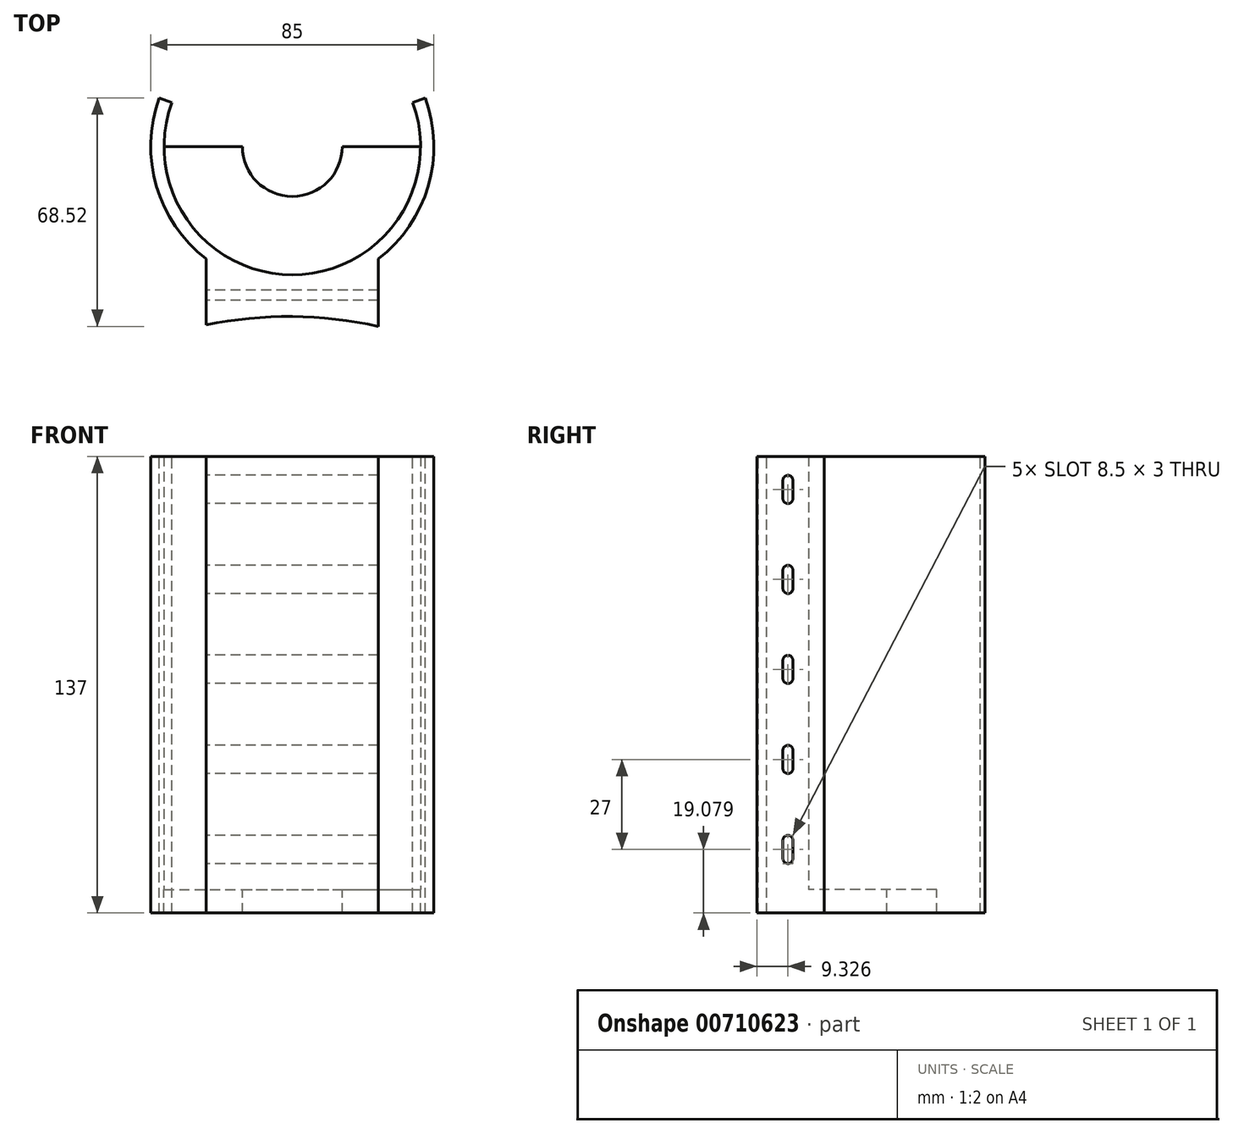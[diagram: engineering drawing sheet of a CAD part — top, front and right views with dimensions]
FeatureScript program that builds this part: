
annotation { "Feature Type Name" : "Feature", "Feature Type Description" : "" }
export const myFeature = defineFeature(function(context is Context, id is Id, definition is map)
    precondition{}
    {
        {
            var Q0;
            Q0=qCreatedBy(makeId("Top.planeOp"),FACE);
            var sketch = newSketch(context, id + "F0", { "sketchPlane" : qUnion([Q0])});
            skCircle(sketch, "E0", {"center": v(0, 0) * mm, "radius": 42.5 * mm});
            skSolve(sketch);
        }
        {
            var Q0;
            Q0=qSketchRegion(id+"F0",true);
            extrude(context, id + "F1", {"entities" : qUnion([Q0]), "depth" : 7 * mm, "offsetDistance" : 25 * mm});
        }
        {
            var Q0;
            Q0=makeQuery(id+"F1.opExtrude","CAP_FACE",FACE,{"disambiguationData":[OSD([sQuery(id+"F0.wireOp",EDGE,"E0")])],"isStart":false});
            var sketch = newSketch(context, id + "F2", { "sketchPlane" : qUnion([Q0])});
            skCircle(sketch, "E1", {"center": v(0, 0) * mm, "radius": 15 * mm});
            skSolve(sketch);
        }
        {
            var Q0;
            Q0=makeQuery(id+"F2.imprint","IMPRINT",FACE,{"disambiguationData":[TD([[makeQuery(id+"F2.imprint","IMPRINT",EDGE,{"derivedFrom":sQuery(id+"F2.wireOp",EDGE,"E1")}),1.0]])]});
            extrude(context, id + "F3", {"entities" : qUnion([Q0]), "operationType" : NewBodyOperationType.REMOVE, "oppositeDirection" : true, "depth" : 25 * mm, "offsetDistance" : 25 * mm});
        }
        {
            var Q0;
            Q0=makeQuery(id+"F1.opExtrude","CAP_FACE",FACE,{"disambiguationData":[OSD([sQuery(id+"F0.wireOp",EDGE,"E0")])],"isStart":false});
            var sketch = newSketch(context, id + "F4", { "sketchPlane" : qUnion([Q0])});
            skCircle(sketch, "E2", {"center": v(0, 0) * mm, "radius": 38.5 * mm});
            skCircle(sketch, "E3", {"center": v(0, 0) * mm, "radius": 42.5 * mm});
            skSolve(sketch);
        }
        {
            var Q0;
            Q0=qSketchRegion(id+"F4",true);
            extrude(context, id + "F5", {"entities" : qUnion([Q0]), "operationType" : NewBodyOperationType.ADD, "depth" : 130 * mm, "offsetDistance" : 25 * mm});
        }
        {
            var Q0;
            Q0=makeQuery(id+"F5.opExtrude","CAP_FACE",FACE,{"disambiguationData":[OSD([sQuery(id+"F4.wireOp",EDGE,"E2"),sQuery(id+"F4.wireOp",EDGE,"E3")])],"isStart":false});
            var sketch = newSketch(context, id + "F6", { "sketchPlane" : qUnion([Q0])});
            skCircle(sketch, "E4.0", {"center": v(0, 0) * mm, "radius": 38.5 * mm});
            skCircle(sketch, "E5.0", {"center": v(0, 0) * mm, "radius": 42.5 * mm});
            skLineSegment(sketch, "E6", {"start": v(-39.94, -14.54) * mm, "end": v(-35.24, -12.83) * mm});
            skLineSegment(sketch, "E7", {"start": v(0, 0) * mm, "end": v(0, 42.5) * mm});
            skLineSegment(sketch, "E8.MirrorCS", {"start": v(-39.94, 14.54) * mm, "end": v(-35.24, 12.83) * mm});
            skLineSegment(sketch, "E9", {"start": v(0, 0) * mm, "end": v(-42.5, 0) * mm});
            skLineSegment(sketch, "E10.MirrorCS", {"start": v(-14.54, -39.94) * mm, "end": v(-12.83, -35.24) * mm});
            skLineSegment(sketch, "E11.MirrorCS", {"start": v(14.54, -39.94) * mm, "end": v(12.83, -35.24) * mm});
            skLineSegment(sketch, "E12.MirrorCS", {"start": v(39.94, 14.54) * mm, "end": v(35.24, 12.83) * mm});
            skLineSegment(sketch, "E13.MirrorCS", {"start": v(39.94, -14.54) * mm, "end": v(35.24, -12.83) * mm});
            skLineSegment(sketch, "E14.MirrorCS", {"start": v(-14.54, 39.94) * mm, "end": v(-12.83, 35.24) * mm});
            skLineSegment(sketch, "E15.MirrorCS", {"start": v(14.54, 39.94) * mm, "end": v(12.83, 35.24) * mm});
            skSolve(sketch);
        }
        {
            var Q0;
            {var subQ0=sQuery(id+"F6.wireOp",EDGE,"E8.MirrorCS");Q0=makeQuery(id+"F6.imprint","IMPRINT",FACE,{"disambiguationData":[TD([[makeQuery(id+"F6.imprint","IMPRINT",EDGE,{"derivedFrom":subQ0}),1.0]])]});}
            var Q1;
            {var subQ0=sQuery(id+"F6.wireOp",EDGE,"E15.MirrorCS");var subQ1=sQuery(id+"F6.wireOp",EDGE,"E4.0");var subQ2=makeQuery(id+"F6.imprint","INTERSECT",VERTEX,{"derivedFrom":[subQ1,subQ0]});Q1=makeQuery(id+"F6.imprint","IMPRINT",FACE,{"disambiguationData":[TD([[makeQuery(id+"F6.imprint","IMPRINT",EDGE,{"disambiguationData":[TD([[subQ2,1.0]])],"derivedFrom":subQ1}),-1.0]])]});}
            var Q2;
            {var subQ0=sQuery(id+"F6.wireOp",EDGE,"E15.MirrorCS");var subQ1=sQuery(id+"F6.wireOp",EDGE,"E4.0");var subQ2=makeQuery(id+"F6.imprint","INTERSECT",VERTEX,{"derivedFrom":[subQ1,subQ0]});Q2=makeQuery(id+"F6.imprint","IMPRINT",FACE,{"disambiguationData":[TD([[makeQuery(id+"F6.imprint","IMPRINT",EDGE,{"disambiguationData":[TD([[subQ2,-1.0]])],"derivedFrom":subQ1}),-1.0]])]});}
            var Q3;
            {var subQ0=sQuery(id+"F6.wireOp",EDGE,"E14.MirrorCS");var subQ1=sQuery(id+"F6.wireOp",EDGE,"E4.0");var subQ2=makeQuery(id+"F6.imprint","INTERSECT",VERTEX,{"derivedFrom":[subQ1,subQ0]});Q3=makeQuery(id+"F6.imprint","IMPRINT",FACE,{"disambiguationData":[TD([[makeQuery(id+"F6.imprint","IMPRINT",EDGE,{"disambiguationData":[TD([[subQ2,1.0]])],"derivedFrom":subQ1}),-1.0]])]});}
            var Q4;
            Q4=makeQuery(id+"F1.opExtrude","CAP_FACE",FACE,{"disambiguationData":[OSD([sQuery(id+"F0.wireOp",EDGE,"E0")])],"isStart":false});
            extrude(context, id + "F7", {"entities" : qUnion([Q0, Q1, Q2, Q3]), "operationType" : NewBodyOperationType.REMOVE, "endBound" : BoundingType.UP_TO_SURFACE, "oppositeDirection" : true, "depth" : 25 * mm, "endBoundEntityFace" : qUnion([Q4]), "offsetDistance" : 25 * mm});
        }
        {
            var Q0;
            Q0=makeQuery(id+"F5.opExtrude","CAP_FACE",FACE,{"disambiguationData":[OSD([sQuery(id+"F4.wireOp",EDGE,"E2"),sQuery(id+"F4.wireOp",EDGE,"E3")])],"isStart":false});
            var sketch = newSketch(context, id + "F8", { "sketchPlane" : qUnion([Q0])});
            skLineSegment(sketch, "E16", {"start": v(-44.89, 0) * mm, "end": v(48.54, 0) * mm});
            skLineSegment(sketch, "E17", {"start": v(48.54, 0) * mm, "end": v(48.54, 50.13) * mm});
            skLineSegment(sketch, "E18", {"start": v(48.54, 50.13) * mm, "end": v(-44.89, 50.13) * mm});
            skLineSegment(sketch, "E19", {"start": v(-44.89, 50.13) * mm, "end": v(-44.89, 0) * mm});
            skSolve(sketch);
        }
        {
            var Q0;
            {var subQ9=sQuery(id+"F8.wireOp",EDGE,"E17");Q0=makeQuery(id+"F8.imprint","IMPRINT",FACE,{"disambiguationData":[TD([[makeQuery(id+"F8.imprint","IMPRINT",EDGE,{"derivedFrom":subQ9}),1.0]])]});}
            var Q1;
            {var subQ5=makeQuery(id+"F7.boolean.opBoolean","COPY",EDGE,{"derivedFrom":makeQuery(id+"F7.opExtrude","CAP_EDGE",EDGE,{"disambiguationData":[OSD([sQuery(id+"F6.wireOp",EDGE,"E8.MirrorCS")])],"isStart":true})});Q1=makeQuery(id+"F8.imprint","IMPRINT",FACE,{"disambiguationData":[TD([[makeQuery(id+"F8.imprint","IMPRINT",EDGE,{"derivedFrom":subQ5}),-1.0]])]});}
            var Q2;
            {var subQ5=makeQuery(id+"F7.boolean.opBoolean","COPY",EDGE,{"derivedFrom":makeQuery(id+"F7.opExtrude","CAP_EDGE",EDGE,{"disambiguationData":[OSD([sQuery(id+"F6.wireOp",EDGE,"E12.MirrorCS")])],"isStart":true})});Q2=makeQuery(id+"F8.imprint","IMPRINT",FACE,{"disambiguationData":[TD([[makeQuery(id+"F8.imprint","IMPRINT",EDGE,{"derivedFrom":subQ5}),1.0]])]});}
            extrude(context, id + "F9", {"entities" : qUnion([Q0, Q1, Q2]), "operationType" : NewBodyOperationType.REMOVE, "endBound" : BoundingType.THROUGH_ALL, "oppositeDirection" : true, "depth" : 25 * mm, "offsetDistance" : 25 * mm});
        }
        {
            var Q0;
            Q0=makeQuery(id+"F5.opExtrude","CAP_FACE",FACE,{"disambiguationData":[OSD([sQuery(id+"F4.wireOp",EDGE,"E2"),sQuery(id+"F4.wireOp",EDGE,"E3")])],"isStart":false});
            var sketch = newSketch(context, id + "F10", { "sketchPlane" : qUnion([Q0])});
            skArc(sketch, "E20.0", {"start": v(-25.84, -33.74) * mm, "mid": v(18.81, -38.1) * mm, "end": v(42.5, 0) * mm});
            skLineSegment(sketch, "E21.0", {"start": v(-25.84, -33.74) * mm, "end": v(-25.84, -53.5) * mm});
            skPoint(sketch, "E22.orphan", {"position": v(-42.5, 0) * mm});
            skLineSegment(sketch, "E23.MirrorCS", {"start": v(25.84, -33.74) * mm, "end": v(25.84, -53.98) * mm});
            skArc(sketch, "E24", {"start": v(25.84, -53.98) * mm, "mid": v(0.02, -51.03) * mm, "end": v(-25.84, -53.5) * mm});
            skSolve(sketch);
        }
        {
            var Q0;
            Q0=qSketchRegion(id+"F10",true);
            var Q1;
            Q1=makeQuery(id+"F1.opExtrude","CAP_FACE",FACE,{"disambiguationData":[OSD([sQuery(id+"F0.wireOp",EDGE,"E0")])],"isStart":true});
            extrude(context, id + "F11", {"entities" : qUnion([Q0]), "operationType" : NewBodyOperationType.ADD, "endBound" : BoundingType.UP_TO_SURFACE, "oppositeDirection" : true, "depth" : 47.1 * mm, "endBoundEntityFace" : qUnion([Q1]), "offsetDistance" : 25 * mm});
        }
        {
            var Q0;
            Q0=makeQuery(id+"F11.opExtrude","SWEPT_FACE",FACE,{"disambiguationData":[OSD([sQuery(id+"F10.wireOp",EDGE,"E21.0")])]});
            var sketch = newSketch(context, id + "F12", { "sketchPlane" : qUnion([Q0])});
            skLineSegment(sketch, "E25", {"start": v(46.15, 129.83) * mm, "end": v(46.15, 124.33) * mm});
            skLineSegment(sketch, "E26.0", {"start": v(43.15, 129.83) * mm, "end": v(43.15, 124.33) * mm});
            skArc(sketch, "E27", {"start": v(46.15, 129.83) * mm, "mid": v(44.65, 131.33) * mm, "end": v(43.15, 129.83) * mm});
            skArc(sketch, "E28", {"start": v(43.15, 124.33) * mm, "mid": v(44.65, 122.83) * mm, "end": v(46.15, 124.33) * mm});
            skArc(sketch, "E29.1.0.0", {"start": v(46.15, 102.83) * mm, "mid": v(44.65, 104.33) * mm, "end": v(43.15, 102.83) * mm});
            skLineSegment(sketch, "E29.1.0.1", {"start": v(46.15, 102.83) * mm, "end": v(46.15, 97.33) * mm});
            skLineSegment(sketch, "E29.1.0.2", {"start": v(43.15, 102.83) * mm, "end": v(43.15, 97.33) * mm});
            skArc(sketch, "E29.1.0.3", {"start": v(43.15, 97.33) * mm, "mid": v(44.65, 95.83) * mm, "end": v(46.15, 97.33) * mm});
            skArc(sketch, "E29.2.0.0", {"start": v(46.15, 75.83) * mm, "mid": v(44.65, 77.33) * mm, "end": v(43.15, 75.83) * mm});
            skLineSegment(sketch, "E29.2.0.1", {"start": v(46.15, 75.83) * mm, "end": v(46.15, 70.33) * mm});
            skLineSegment(sketch, "E29.2.0.2", {"start": v(43.15, 75.83) * mm, "end": v(43.15, 70.33) * mm});
            skArc(sketch, "E29.2.0.3", {"start": v(43.15, 70.33) * mm, "mid": v(44.65, 68.83) * mm, "end": v(46.15, 70.33) * mm});
            skLineSegment(sketch, "E29.direction1", {"start": v(44.65, 124.33) * mm, "end": v(44.65, 97.33) * mm, "construction": true});
            skArc(sketch, "E30.0.3.0", {"start": v(46.15, 48.83) * mm, "mid": v(44.65, 50.33) * mm, "end": v(43.15, 48.83) * mm});
            skLineSegment(sketch, "E30.4.3.0", {"start": v(46.15, 48.83) * mm, "end": v(46.15, 43.33) * mm});
            skLineSegment(sketch, "E30.7.3.0", {"start": v(43.15, 48.83) * mm, "end": v(43.15, 43.33) * mm});
            skArc(sketch, "E30.10.3.0", {"start": v(43.15, 43.33) * mm, "mid": v(44.65, 41.83) * mm, "end": v(46.15, 43.33) * mm});
            skArc(sketch, "E30.0.4.0", {"start": v(46.15, 21.83) * mm, "mid": v(44.65, 23.33) * mm, "end": v(43.15, 21.83) * mm});
            skLineSegment(sketch, "E30.4.4.0", {"start": v(46.15, 21.83) * mm, "end": v(46.15, 16.33) * mm});
            skLineSegment(sketch, "E30.7.4.0", {"start": v(43.15, 21.83) * mm, "end": v(43.15, 16.33) * mm});
            skArc(sketch, "E30.10.4.0", {"start": v(43.15, 16.33) * mm, "mid": v(44.65, 14.83) * mm, "end": v(46.15, 16.33) * mm});
            skSolve(sketch);
        }
        {
            var Q0;
            Q0 = qSketchRegion(id + "F12", true);
            extrude(context, id + "F13", {"entities" : qUnion([Q0]), "operationType" : NewBodyOperationType.REMOVE, "endBound" : BoundingType.THROUGH_ALL, "oppositeDirection" : true, "depth" : 25 * mm, "offsetDistance" : 25 * mm});
        }
    });
